# Revit family: Slide
name_source: partatom
category: Lighting Fixtures
units: mm (PartAtom-declared; Revit-internal decimal feet)

## family parameters
Cut with Voids When Loaded = No
Host = Face
Light Source = Yes
OmniClass Number = 23.80.70.14.21
OmniClass Title = Street and Roadway Lighting
Part Type = Normal
Room Calculation Point = No
Round Connector Dimension = Use Diameter
Shared = No

## types (12) — shared parameters
Apparent Load = 55 VA
Color Filter = 16777215
Default Elevation = 48"
Description = The direct optical system give the designer
3 different LED wattages and 6
different lighting distribution patterns.
Dimming Lamp Color Temperature Shift = <None>
Emit Shape Visible in Rendering = No
Emit from Rectangle Length = 8"
Emit from Rectangle Width = 8"
Lamp = Each Beacon Slide luminaire is supplied with an
Optical one piece cartridge system consisting of an
LED engine, LED lamps, optics, gasket and stamped
stainless steel bezel.
Load Classification = Lighting
Manufacturer = Beacon Products
Model = SLIDE(LED)
Photometric Web File = 24NB-55-T4.ies
Pole Height = 144"
Power Factor = 0.92
Tilt Angle = 90.00°
URL = https://www.currentlighting.com
Voltage = 120 V
Wattage Comments = Luminaires are equipped with an LED driver that accepts 100V through 277V, 50 Hz to 60 Hz (UNIV), or a driver that accepts 347V or 480V input.

## per-type parameters (varying)
| type | Product Material | Shade Option |
| Basic Black Textured | Paint-Basic Black | Shade : Sloped |
| Black Matte Textured | Paint-Black Matte | Shade : Sloped |
| Bronze Textured | Paint-Bronze | Shade : Sloped |
| Dark Bronze Textured | Paint-Dark Bronze | Shade : Sloped |
| Dark Platinum Smooth | Paint-Dark Platinum Smooth | Shade : Sloped |
| Gray Smooth | Paint-Gray Smooth | Shade : Sloped |
| Green Textured | Paint-Green | Shade : Sloped |
| Metallic Bronze Textured | Paint-Metallic Bronze | Shade : Sloped |
| Metallic Silver Textured | Paint-Metallic Silver | Shade : Sloped |
| Metallic Titanium Textured | Paint-Metallic Titanium | Shade : Sloped |
| Old World Iron | Paint-Old World Iron | Shade : Sloped |
| White Texture | Paint-White | Shade : Curved |

## geometry (parser evidence)
native form markers: Sweep x4
no freeform markers — native parametric forms only
